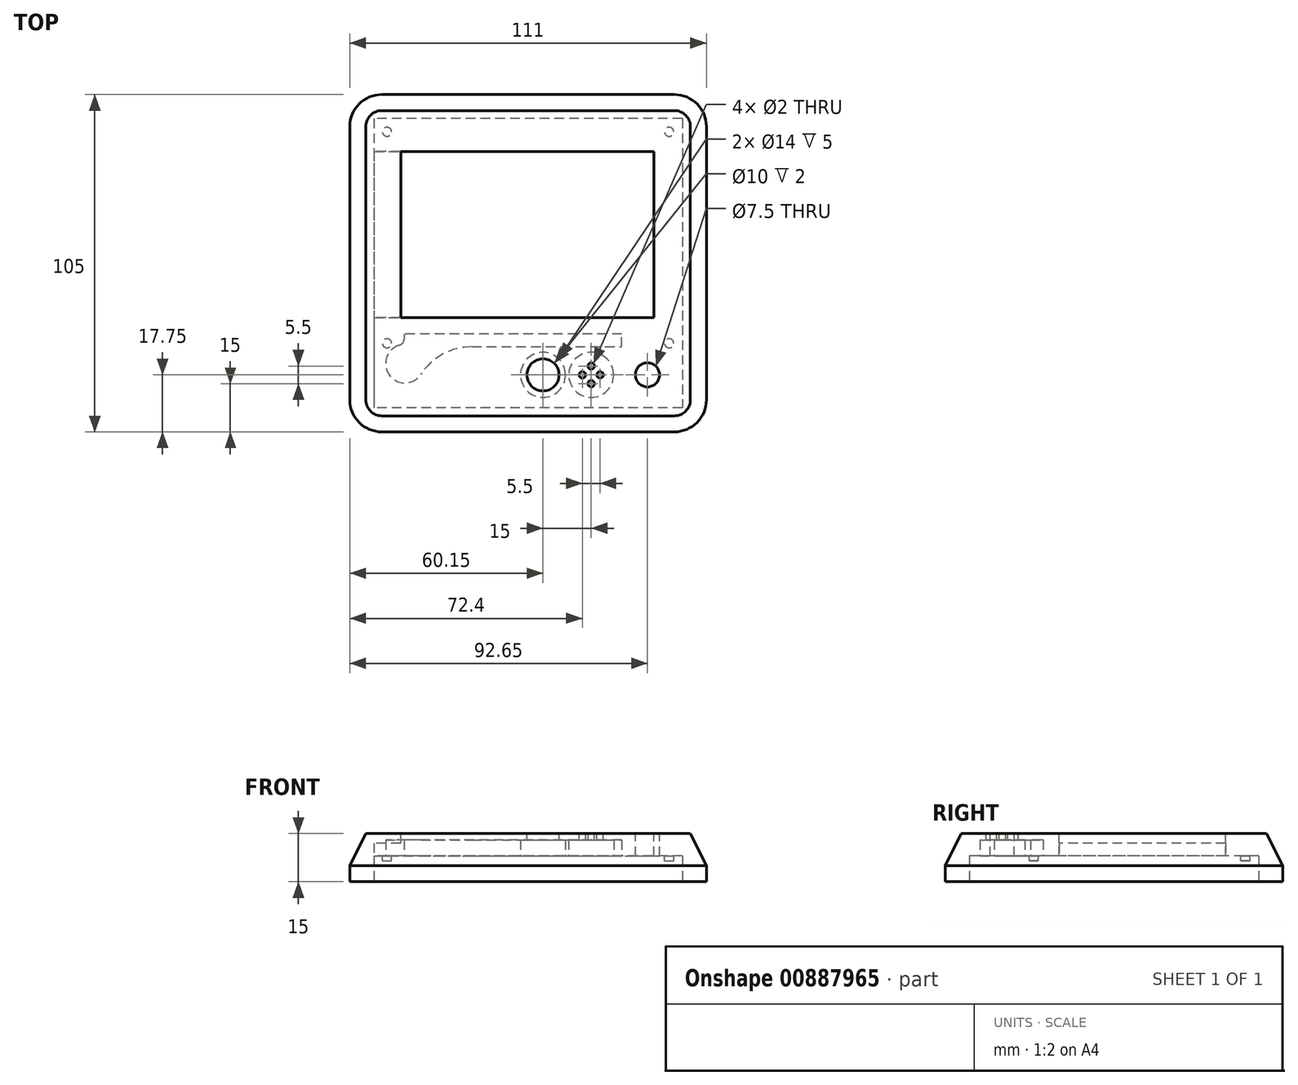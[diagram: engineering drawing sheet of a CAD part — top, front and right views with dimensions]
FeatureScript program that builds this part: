
annotation { "Feature Type Name" : "Feature", "Feature Type Description" : "" }
export const myFeature = defineFeature(function(context is Context, id is Id, definition is map)
    precondition{}
    {
        {
            var Q0;
            Q0=qCreatedBy(makeId("Top.planeOp"),FACE);
            var sketch = newSketch(context, id + "F0", { "sketchPlane" : qUnion([Q0])});
            skLineSegment(sketch, "E0.bottom", {"start": v(-45.5, 47.5) * mm, "end": v(45.5, 47.5) * mm});
            skLineSegment(sketch, "E0.top", {"start": v(-45.5, -47.5) * mm, "end": v(45.5, -47.5) * mm});
            skLineSegment(sketch, "E0.left", {"start": v(-50.5, 42.5) * mm, "end": v(-50.5, -42.5) * mm});
            skLineSegment(sketch, "E0.right", {"start": v(50.5, 42.5) * mm, "end": v(50.5, -42.5) * mm});
            skPoint(sketch, "E1.visualSharp", {"position": v(-50.5, 47.5) * mm});
            skArc(sketch, "E1.filletArc", {"start": v(-45.5, 47.5) * mm, "mid": v(-49.04, 46.04) * mm, "end": v(-50.5, 42.5) * mm});
            skPoint(sketch, "E2.visualSharp", {"position": v(50.5, 47.5) * mm});
            skArc(sketch, "E2.filletArc", {"start": v(50.5, 42.5) * mm, "mid": v(49.04, 46.04) * mm, "end": v(45.5, 47.5) * mm});
            skPoint(sketch, "E3.visualSharp", {"position": v(-50.5, -47.5) * mm});
            skArc(sketch, "E3.filletArc", {"start": v(-50.5, -42.5) * mm, "mid": v(-49.04, -46.04) * mm, "end": v(-45.5, -47.5) * mm});
            skPoint(sketch, "E4.visualSharp", {"position": v(50.5, -47.5) * mm});
            skArc(sketch, "E4.filletArc", {"start": v(45.5, -47.5) * mm, "mid": v(49.04, -46.04) * mm, "end": v(50.5, -42.5) * mm});
            skLineSegment(sketch, "E5.bottom", {"start": v(-39.6, 34.75) * mm, "end": v(39.15, 34.75) * mm});
            skLineSegment(sketch, "E5.top", {"start": v(-39.6, -17) * mm, "end": v(39.15, -17) * mm});
            skLineSegment(sketch, "E5.left", {"start": v(-39.6, 34.75) * mm, "end": v(-39.6, -17) * mm});
            skLineSegment(sketch, "E5.right", {"start": v(39.15, 34.75) * mm, "end": v(39.15, -17) * mm});
            skCircle(sketch, "E6", {"center": v(37.15, -34.75) * mm, "radius": 3.75 * mm});
            skCircle(sketch, "E7", {"center": v(4.65, -34.75) * mm, "radius": 5 * mm});
            skCircle(sketch, "E8", {"center": v(19.65, -32) * mm, "radius": 1 * mm});
            skCircle(sketch, "E9", {"center": v(19.65, -37.5) * mm, "radius": 1 * mm});
            skCircle(sketch, "E10", {"center": v(16.9, -34.75) * mm, "radius": 1 * mm});
            skCircle(sketch, "E11", {"center": v(22.4, -34.75) * mm, "radius": 1 * mm});
            skCircle(sketch, "E12", {"center": v(-38.35, -31.25) * mm, "radius": 3.25 * mm});
            skLineSegment(sketch, "E13.bottom", {"start": v(-46.5, 43.5) * mm, "end": v(46.5, 43.5) * mm, "construction": true});
            skLineSegment(sketch, "E13.top", {"start": v(-46.5, -43.5) * mm, "end": v(46.5, -43.5) * mm, "construction": true});
            skLineSegment(sketch, "E13.left", {"start": v(-46.5, 43.5) * mm, "end": v(-46.5, -43.5) * mm, "construction": true});
            skLineSegment(sketch, "E13.right", {"start": v(46.5, 43.5) * mm, "end": v(46.5, -43.5) * mm, "construction": true});
            skCircle(sketch, "E14", {"center": v(19.65, -34.75) * mm, "radius": 2.75 * mm, "construction": true});
            skCircle(sketch, "E15", {"center": v(-43.9, 40.9) * mm, "radius": 1.73 * mm});
            skCircle(sketch, "E16", {"center": v(43.9, 40.9) * mm, "radius": 1.73 * mm});
            skCircle(sketch, "E17", {"center": v(43.9, -24.9) * mm, "radius": 1.73 * mm});
            skCircle(sketch, "E18", {"center": v(-43.9, -24.9) * mm, "radius": 1.73 * mm});
            skSolve(sketch);
        }
        {
            var Q0;
            Q0=qCreatedBy(makeId("Top.planeOp"),FACE);
            var sketch = newSketch(context, id + "F1", { "sketchPlane" : qUnion([Q0])});
            skArc(sketch, "E19.0", {"start": v(-45.5, 52.5) * mm, "mid": v(-52.57, 49.57) * mm, "end": v(-55.5, 42.5) * mm});
            skLineSegment(sketch, "E19.1", {"start": v(-45.5, 52.5) * mm, "end": v(45.5, 52.5) * mm});
            skLineSegment(sketch, "E19.2", {"start": v(-55.5, 42.5) * mm, "end": v(-55.5, -42.5) * mm});
            skArc(sketch, "E19.3", {"start": v(55.5, 42.5) * mm, "mid": v(52.57, 49.57) * mm, "end": v(45.5, 52.5) * mm});
            skArc(sketch, "E19.4", {"start": v(-55.5, -42.5) * mm, "mid": v(-52.57, -49.57) * mm, "end": v(-45.5, -52.5) * mm});
            skLineSegment(sketch, "E19.5", {"start": v(-45.5, -52.5) * mm, "end": v(45.5, -52.5) * mm});
            skArc(sketch, "E19.6", {"start": v(45.5, -52.5) * mm, "mid": v(52.57, -49.57) * mm, "end": v(55.5, -42.5) * mm});
            skLineSegment(sketch, "E19.7", {"start": v(55.5, 42.5) * mm, "end": v(55.5, -42.5) * mm});
            skSolve(sketch);
        }
        {
            var Q0;
            Q0 = qSketchRegion(id + "F1", true);
            extrude(context, id + "F2", {"entities" : qUnion([Q0]), "oppositeDirection" : true, "depth" : 15 * mm, "offsetDistance" : 25 * mm});
        }
        {
            var Q0;
            Q0=makeQuery(id+"F2.opExtrude","CAP_EDGE",EDGE,{"disambiguationData":[OSD([sQuery(id+"F1.wireOp",EDGE,"E19.2")])],"isStart":true});
            chamfer(context, id + "F3", {"entities" : qUnion([Q0]), "chamferType" : ChamferType.TWO_OFFSETS, "width1" : 5 * mm, "oppositeDirection" : false, "width2" : 10 * mm, "tangentPropagation" : true});
        }
        {
            var Q0;
            Q0=qCreatedBy(makeId("Top.planeOp"),FACE);
            var sketch = newSketch(context, id + "F4", { "sketchPlane" : qUnion([Q0])});
            skLineSegment(sketch, "E20.0", {"start": v(-39.6, 34.75) * mm, "end": v(-39.6, -17) * mm});
            skLineSegment(sketch, "E21.0", {"start": v(-39.6, 34.75) * mm, "end": v(39.15, 34.75) * mm});
            skLineSegment(sketch, "E22.0", {"start": v(39.15, 34.75) * mm, "end": v(39.15, -17) * mm});
            skLineSegment(sketch, "E23.0", {"start": v(-39.6, -17) * mm, "end": v(39.15, -17) * mm});
            skCircle(sketch, "E24.0", {"center": v(4.65, -34.75) * mm, "radius": 5 * mm});
            skCircle(sketch, "E25.0", {"center": v(37.15, -34.75) * mm, "radius": 3.75 * mm});
            skCircle(sketch, "E26.0", {"center": v(16.9, -34.75) * mm, "radius": 1 * mm});
            skCircle(sketch, "E27.0", {"center": v(19.65, -32) * mm, "radius": 1 * mm});
            skCircle(sketch, "E28.0", {"center": v(22.4, -34.75) * mm, "radius": 1 * mm});
            skCircle(sketch, "E29.0", {"center": v(19.65, -37.5) * mm, "radius": 1 * mm});
            skSolve(sketch);
        }
        {
            var Q0;
            Q0 = qSketchRegion(id + "F4", true);
            extrude(context, id + "F5", {"entities" : qUnion([Q0]), "operationType" : NewBodyOperationType.REMOVE, "endBound" : BoundingType.THROUGH_ALL, "oppositeDirection" : true, "depth" : 25 * mm, "offsetDistance" : 25 * mm});
        }
        {
            var Q0;
            Q0=makeQuery(id+"F2.opExtrude","CAP_FACE",FACE,{"disambiguationData":[OSD([sQuery(id+"F1.wireOp",EDGE,"E19.0"),sQuery(id+"F1.wireOp",EDGE,"E19.1"),sQuery(id+"F1.wireOp",EDGE,"E19.2"),sQuery(id+"F1.wireOp",EDGE,"E19.3"),sQuery(id+"F1.wireOp",EDGE,"E19.4"),sQuery(id+"F1.wireOp",EDGE,"E19.5"),sQuery(id+"F1.wireOp",EDGE,"E19.6"),sQuery(id+"F1.wireOp",EDGE,"E19.7")])],"isStart":false});
            var sketch = newSketch(context, id + "F6", { "sketchPlane" : qUnion([Q0])});
            skLineSegment(sketch, "E30.bottom", {"start": v(48, -45) * mm, "end": v(-48, -45) * mm});
            skLineSegment(sketch, "E30.top", {"start": v(48, 45) * mm, "end": v(-48, 45) * mm});
            skLineSegment(sketch, "E30.left", {"start": v(48, -45) * mm, "end": v(48, 45) * mm});
            skLineSegment(sketch, "E30.right", {"start": v(-48, -45) * mm, "end": v(-48, 45) * mm});
            skSolve(sketch);
        }
        {
            var Q0;
            Q0 = qSketchRegion(id + "F6", true);
            extrude(context, id + "F7", {"entities" : qUnion([Q0]), "operationType" : NewBodyOperationType.REMOVE, "oppositeDirection" : true, "depth" : 8 * mm, "offsetDistance" : 25 * mm});
        }
        {
            var Q0;
            Q0=makeQuery(id+"F7.boolean.opBoolean","COPY",FACE,{"derivedFrom":makeQuery(id+"F7.opExtrude","CAP_FACE",FACE,{"disambiguationData":[OSD([sQuery(id+"F6.wireOp",EDGE,"E30.bottom"),sQuery(id+"F6.wireOp",EDGE,"E30.top"),sQuery(id+"F6.wireOp",EDGE,"E30.left"),sQuery(id+"F6.wireOp",EDGE,"E30.right")])],"isStart":false})});
            var sketch = newSketch(context, id + "F8", { "sketchPlane" : qUnion([Q0])});
            skPoint(sketch, "E31.0", {"position": v(43.9, -40.9) * mm});
            skPoint(sketch, "E32.0", {"position": v(-43.9, -40.9) * mm});
            skPoint(sketch, "E33.0", {"position": v(-43.9, 24.9) * mm});
            skPoint(sketch, "E34.0", {"position": v(43.9, 24.9) * mm});
            skCircle(sketch, "E35", {"center": v(43.9, -40.9) * mm, "radius": 1.43 * mm});
            skCircle(sketch, "E36", {"center": v(-43.9, -40.9) * mm, "radius": 1.43 * mm});
            skCircle(sketch, "E37", {"center": v(-43.9, 24.9) * mm, "radius": 1.43 * mm});
            skCircle(sketch, "E38", {"center": v(43.9, 24.9) * mm, "radius": 1.43 * mm});
            skSolve(sketch);
        }
        {
            var Q0;
            Q0 = qSketchRegion(id + "F8", true);
            extrude(context, id + "F9", {"entities" : qUnion([Q0]), "operationType" : NewBodyOperationType.ADD, "depth" : 1.5 * mm, "offsetDistance" : 25 * mm});
        }
        {
            var Q0;
            Q0=makeQuery(id+"F7.boolean.opBoolean","COPY",FACE,{"derivedFrom":makeQuery(id+"F7.opExtrude","CAP_FACE",FACE,{"disambiguationData":[OSD([sQuery(id+"F6.wireOp",EDGE,"E30.bottom"),sQuery(id+"F6.wireOp",EDGE,"E30.top"),sQuery(id+"F6.wireOp",EDGE,"E30.left"),sQuery(id+"F6.wireOp",EDGE,"E30.right")])],"isStart":false})});
            var sketch = newSketch(context, id + "F10", { "sketchPlane" : qUnion([Q0])});
            skLineSegment(sketch, "E39.bottom", {"start": v(-39.6, 17) * mm, "end": v(-48, 17) * mm});
            skLineSegment(sketch, "E39.top", {"start": v(-39.6, -34.75) * mm, "end": v(-48, -34.75) * mm});
            skLineSegment(sketch, "E39.left", {"start": v(-39.6, 17) * mm, "end": v(-39.6, -34.75) * mm});
            skLineSegment(sketch, "E39.right", {"start": v(-48, 17) * mm, "end": v(-48, -34.75) * mm});
            skSolve(sketch);
        }
        {
            var Q0;
            Q0 = qSketchRegion(id + "F10", true);
            extrude(context, id + "F11", {"entities" : qUnion([Q0]), "operationType" : NewBodyOperationType.REMOVE, "oppositeDirection" : true, "depth" : 4 * mm, "offsetDistance" : 25 * mm});
        }
        {
            var Q0;
            Q0=makeQuery(id+"F7.boolean.opBoolean","COPY",FACE,{"derivedFrom":makeQuery(id+"F7.opExtrude","CAP_FACE",FACE,{"disambiguationData":[OSD([sQuery(id+"F6.wireOp",EDGE,"E30.bottom"),sQuery(id+"F6.wireOp",EDGE,"E30.top"),sQuery(id+"F6.wireOp",EDGE,"E30.left"),sQuery(id+"F6.wireOp",EDGE,"E30.right")])],"isStart":false})});
            var sketch = newSketch(context, id + "F12", { "sketchPlane" : qUnion([Q0])});
            skCircle(sketch, "E40", {"center": v(4.65, 34.75) * mm, "radius": 7 * mm});
            skPoint(sketch, "E41.0", {"position": v(19.65, 34.75) * mm});
            skCircle(sketch, "E42", {"center": v(19.65, 34.75) * mm, "radius": 7 * mm});
            skSolve(sketch);
        }
        {
            var Q0;
            Q0 = qSketchRegion(id + "F12", true);
            extrude(context, id + "F13", {"entities" : qUnion([Q0]), "operationType" : NewBodyOperationType.REMOVE, "oppositeDirection" : true, "depth" : 5 * mm, "offsetDistance" : 25 * mm});
        }
        {
            var Q0;
            Q0=makeQuery(id+"F7.boolean.opBoolean","COPY",FACE,{"derivedFrom":makeQuery(id+"F7.opExtrude","CAP_FACE",FACE,{"disambiguationData":[OSD([sQuery(id+"F6.wireOp",EDGE,"E30.bottom"),sQuery(id+"F6.wireOp",EDGE,"E30.top"),sQuery(id+"F6.wireOp",EDGE,"E30.left"),sQuery(id+"F6.wireOp",EDGE,"E30.right")])],"isStart":false})});
            var sketch = newSketch(context, id + "F14", { "sketchPlane" : qUnion([Q0])});
            skLineSegment(sketch, "E43", {"start": v(29.15, 22) * mm, "end": v(-38.6, 22) * mm});
            skLineSegment(sketch, "E44", {"start": v(-38.6, 22) * mm, "end": v(-38.6, 23.57) * mm});
            skArc(sketch, "E45", {"start": v(-38.6, 23.57) * mm, "mid": v(-39, 24.77) * mm, "end": v(-40.04, 25.5) * mm});
            skArc(sketch, "E46", {"start": v(-33.34, 34.55) * mm, "mid": v(-43.17, 34.82) * mm, "end": v(-40.04, 25.5) * mm});
            skArc(sketch, "E47", {"start": v(-33.34, 34.55) * mm, "mid": v(-26.48, 28.27) * mm, "end": v(-17.47, 26) * mm});
            skLineSegment(sketch, "E48", {"start": v(-17.47, 26) * mm, "end": v(29.15, 26) * mm});
            skLineSegment(sketch, "E49", {"start": v(29.15, 26) * mm, "end": v(29.15, 22) * mm});
            skSolve(sketch);
        }
        {
            var Q0;
            Q0 = qSketchRegion(id + "F14", true);
            extrude(context, id + "F15", {"entities" : qUnion([Q0]), "operationType" : NewBodyOperationType.REMOVE, "oppositeDirection" : true, "depth" : 5 * mm, "offsetDistance" : 25 * mm});
        }
    });
